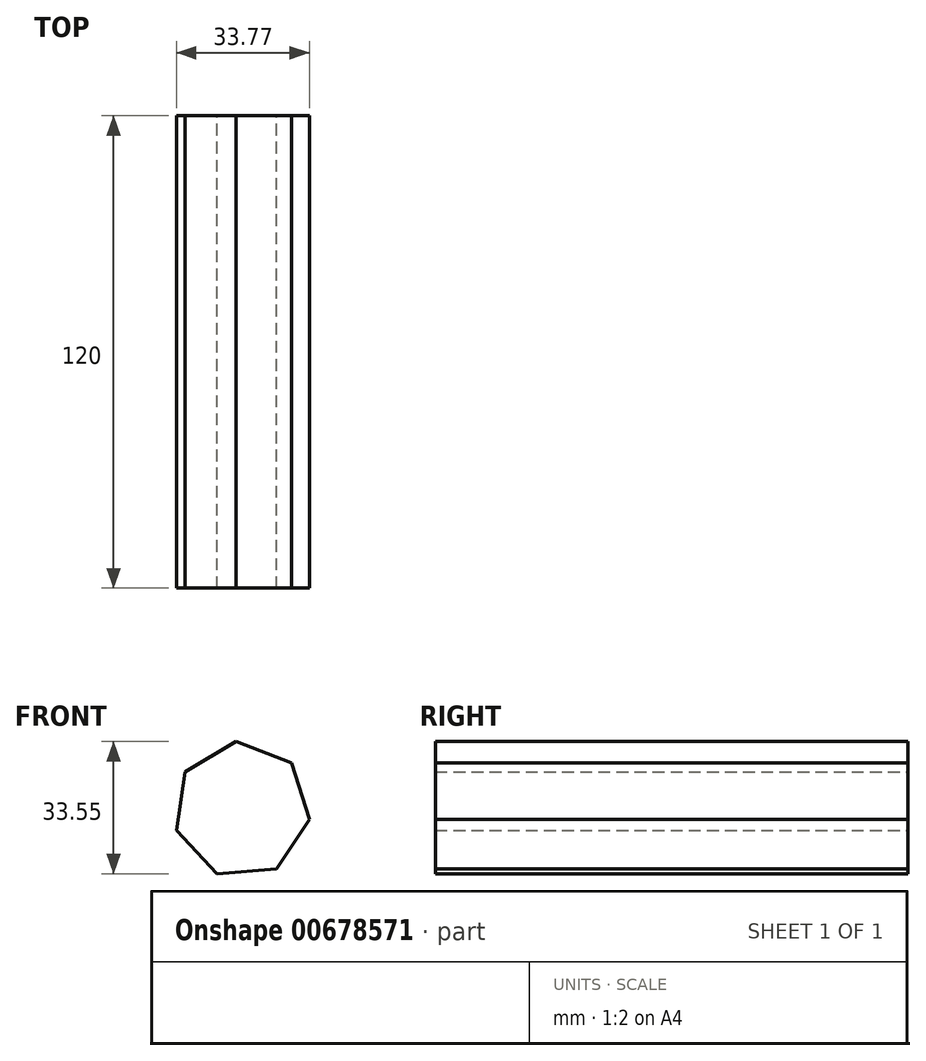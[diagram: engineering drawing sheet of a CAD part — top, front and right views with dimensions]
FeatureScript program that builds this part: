
annotation { "Feature Type Name" : "Feature", "Feature Type Description" : "" }
export const myFeature = defineFeature(function(context is Context, id is Id, definition is map)
    precondition{}
    {
        {
            var Q0;
            Q0=qCreatedBy(makeId("Front.planeOp"),FACE);
            var sketch = newSketch(context, id + "F0", { "sketchPlane" : qUnion([Q0])});
            skLineSegment(sketch, "E0.0", {"start": v(17.2, -2.44) * mm, "end": v(8.82, -14.97) * mm});
            skLineSegment(sketch, "E0.1", {"start": v(8.82, -14.97) * mm, "end": v(-6.2, -16.23) * mm});
            skLineSegment(sketch, "E0.2", {"start": v(-6.2, -16.23) * mm, "end": v(-16.56, -5.27) * mm});
            skLineSegment(sketch, "E0.3", {"start": v(-16.56, -5.27) * mm, "end": v(-14.45, 9.66) * mm});
            skLineSegment(sketch, "E0.4", {"start": v(-14.45, 9.66) * mm, "end": v(-1.45, 17.32) * mm});
            skLineSegment(sketch, "E0.5", {"start": v(-1.45, 17.32) * mm, "end": v(12.63, 11.93) * mm});
            skLineSegment(sketch, "E0.6", {"start": v(12.63, 11.93) * mm, "end": v(17.2, -2.44) * mm});
            skSolve(sketch);
        }
        {
            var Q0;
            Q0=makeQuery(id+"F0.imprint","IMPRINT",FACE,{"disambiguationData":[TD([[makeQuery(id+"F0.imprint","IMPRINT",EDGE,{"derivedFrom":sQuery(id+"F0.wireOp",EDGE,"E0.0")}),-1.0]])]});
            extrude(context, id + "F1", {"entities" : qUnion([Q0]), "depth" : 120 * mm, "offsetDistance" : 25 * mm});
        }
    });
